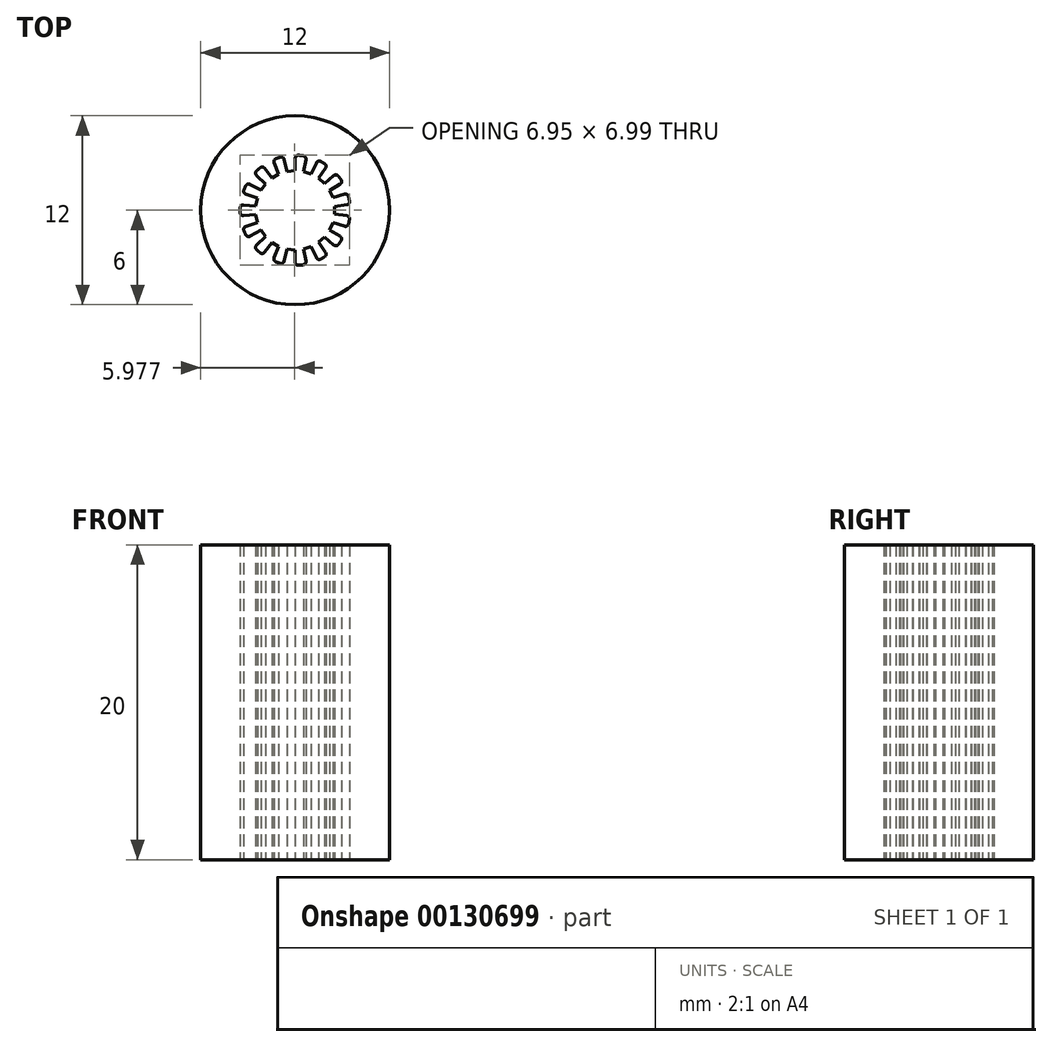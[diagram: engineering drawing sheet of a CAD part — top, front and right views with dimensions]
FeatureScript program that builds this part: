
annotation { "Feature Type Name" : "Feature", "Feature Type Description" : "" }
export const myFeature = defineFeature(function(context is Context, id is Id, definition is map)
    precondition{}
    {
        {
            var Q0;
            Q0=qCreatedBy(makeId("Top.planeOp"),FACE);
            var sketch = newSketch(context, id + "F0", { "sketchPlane" : qUnion([Q0])});
            skCircle(sketch, "E0", {"center": v(0, 0) * mm, "radius": 6 * mm});
            skLineSegment(sketch, "E1", {"start": v(2.5, 0) * mm, "end": v(3.5, 0) * mm, "construction": true});
            skLineSegment(sketch, "E2.right", {"start": v(2.5, 0.25) * mm, "end": v(2.5, -0.25) * mm});
            skPoint(sketch, "E2.middle", {"position": v(3, 0) * mm});
            skLineSegment(sketch, "E3", {"start": v(2.5, 0.25) * mm, "end": v(3.28, 0.35) * mm});
            skLineSegment(sketch, "E4", {"start": v(2.5, -0.25) * mm, "end": v(3.28, -0.35) * mm});
            skPoint(sketch, "E5.visualSharp", {"position": v(3.48, 0.37) * mm});
            skArc(sketch, "E5.filletArc", {"start": v(3.28, 0.35) * mm, "mid": v(3.41, 0.43) * mm, "end": v(3.45, 0.58) * mm});
            skPoint(sketch, "E6.visualSharp", {"position": v(3.48, -0.38) * mm});
            skArc(sketch, "E6.filletArc", {"start": v(3.45, -0.58) * mm, "mid": v(3.41, -0.43) * mm, "end": v(3.28, -0.35) * mm});
            skLineSegment(sketch, "E7.1.0", {"start": v(2.4, -0.8) * mm, "end": v(3.14, -1.01) * mm});
            skLineSegment(sketch, "E7.1.1", {"start": v(2.4, -0.8) * mm, "end": v(2.2, -1.25) * mm});
            skArc(sketch, "E7.1.2", {"start": v(2.92, -1.93) * mm, "mid": v(2.95, -1.78) * mm, "end": v(2.85, -1.65) * mm});
            skArc(sketch, "E7.1.3", {"start": v(3.14, -1.01) * mm, "mid": v(3.3, -1) * mm, "end": v(3.39, -0.87) * mm});
            skLineSegment(sketch, "E7.1.4", {"start": v(2.2, -1.25) * mm, "end": v(2.85, -1.65) * mm});
            skLineSegment(sketch, "E7.2.0", {"start": v(1.86, -1.7) * mm, "end": v(2.45, -2.2) * mm});
            skLineSegment(sketch, "E7.2.1", {"start": v(1.86, -1.7) * mm, "end": v(1.5, -2.03) * mm});
            skArc(sketch, "E7.2.2", {"start": v(1.88, -2.95) * mm, "mid": v(1.97, -2.82) * mm, "end": v(1.94, -2.67) * mm});
            skArc(sketch, "E7.2.3", {"start": v(2.45, -2.2) * mm, "mid": v(2.6, -2.25) * mm, "end": v(2.74, -2.18) * mm});
            skLineSegment(sketch, "E7.2.4", {"start": v(1.5, -2.03) * mm, "end": v(1.94, -2.67) * mm});
            skLineSegment(sketch, "E7.3.0", {"start": v(1.01, -2.3) * mm, "end": v(1.35, -3.01) * mm});
            skLineSegment(sketch, "E7.3.1", {"start": v(1.01, -2.3) * mm, "end": v(0.54, -2.46) * mm});
            skArc(sketch, "E7.3.2", {"start": v(0.51, -3.46) * mm, "mid": v(0.65, -3.38) * mm, "end": v(0.68, -3.23) * mm});
            skArc(sketch, "E7.3.3", {"start": v(1.35, -3.01) * mm, "mid": v(1.46, -3.12) * mm, "end": v(1.62, -3.1) * mm});
            skLineSegment(sketch, "E7.3.4", {"start": v(0.54, -2.46) * mm, "end": v(0.68, -3.23) * mm});
            skLineSegment(sketch, "E7.4.0", {"start": v(-0.01, -2.52) * mm, "end": v(0, -3.3) * mm});
            skLineSegment(sketch, "E7.4.1", {"start": v(-0.01, -2.52) * mm, "end": v(-0.51, -2.47) * mm});
            skArc(sketch, "E7.4.2", {"start": v(-0.94, -3.37) * mm, "mid": v(-0.78, -3.35) * mm, "end": v(-0.7, -3.23) * mm});
            skArc(sketch, "E7.4.3", {"start": v(0, -3.3) * mm, "mid": v(0.07, -3.44) * mm, "end": v(0.22, -3.5) * mm});
            skLineSegment(sketch, "E7.4.4", {"start": v(-0.51, -2.47) * mm, "end": v(-0.7, -3.23) * mm});
            skLineSegment(sketch, "E7.5.0", {"start": v(-1.04, -2.3) * mm, "end": v(-1.34, -3.01) * mm});
            skLineSegment(sketch, "E7.5.1", {"start": v(-1.04, -2.3) * mm, "end": v(-1.47, -2.05) * mm});
            skArc(sketch, "E7.5.2", {"start": v(-2.23, -2.7) * mm, "mid": v(-2.08, -2.74) * mm, "end": v(-1.94, -2.67) * mm});
            skArc(sketch, "E7.5.3", {"start": v(-1.34, -3.01) * mm, "mid": v(-1.34, -3.17) * mm, "end": v(-1.22, -3.28) * mm});
            skLineSegment(sketch, "E7.5.4", {"start": v(-1.47, -2.05) * mm, "end": v(-1.94, -2.67) * mm});
            skLineSegment(sketch, "E7.6.0", {"start": v(-1.88, -1.68) * mm, "end": v(-2.45, -2.21) * mm});
            skLineSegment(sketch, "E7.6.1", {"start": v(-1.88, -1.68) * mm, "end": v(-2.18, -1.27) * mm});
            skArc(sketch, "E7.6.2", {"start": v(-3.13, -1.56) * mm, "mid": v(-3.01, -1.66) * mm, "end": v(-2.86, -1.65) * mm});
            skArc(sketch, "E7.6.3", {"start": v(-2.45, -2.21) * mm, "mid": v(-2.51, -2.35) * mm, "end": v(-2.45, -2.5) * mm});
            skLineSegment(sketch, "E7.6.4", {"start": v(-2.18, -1.27) * mm, "end": v(-2.86, -1.65) * mm});
            skLineSegment(sketch, "E7.7.0", {"start": v(-2.4, -0.77) * mm, "end": v(-3.14, -1.02) * mm});
            skLineSegment(sketch, "E7.7.1", {"start": v(-2.4, -0.77) * mm, "end": v(-2.5, -0.28) * mm});
            skArc(sketch, "E7.7.2", {"start": v(-3.5, -0.15) * mm, "mid": v(-3.43, -0.3) * mm, "end": v(-3.28, -0.34) * mm});
            skArc(sketch, "E7.7.3", {"start": v(-3.14, -1.02) * mm, "mid": v(-3.25, -1.13) * mm, "end": v(-3.26, -1.29) * mm});
            skLineSegment(sketch, "E7.7.4", {"start": v(-2.5, -0.28) * mm, "end": v(-3.28, -0.34) * mm});
            skLineSegment(sketch, "E7.8.0", {"start": v(-2.5, 0.28) * mm, "end": v(-3.28, 0.34) * mm});
            skLineSegment(sketch, "E7.8.1", {"start": v(-2.5, 0.28) * mm, "end": v(-2.4, 0.77) * mm});
            skArc(sketch, "E7.8.2", {"start": v(-3.26, 1.29) * mm, "mid": v(-3.25, 1.13) * mm, "end": v(-3.14, 1.02) * mm});
            skArc(sketch, "E7.8.3", {"start": v(-3.28, 0.34) * mm, "mid": v(-3.43, 0.3) * mm, "end": v(-3.5, 0.15) * mm});
            skLineSegment(sketch, "E7.8.4", {"start": v(-2.4, 0.77) * mm, "end": v(-3.14, 1.02) * mm});
            skLineSegment(sketch, "E7.9.0", {"start": v(-2.18, 1.27) * mm, "end": v(-2.86, 1.65) * mm});
            skLineSegment(sketch, "E7.9.1", {"start": v(-2.18, 1.27) * mm, "end": v(-1.88, 1.68) * mm});
            skArc(sketch, "E7.9.2", {"start": v(-2.45, 2.5) * mm, "mid": v(-2.51, 2.35) * mm, "end": v(-2.45, 2.21) * mm});
            skArc(sketch, "E7.9.3", {"start": v(-2.86, 1.65) * mm, "mid": v(-3.01, 1.66) * mm, "end": v(-3.13, 1.56) * mm});
            skLineSegment(sketch, "E7.9.4", {"start": v(-1.88, 1.68) * mm, "end": v(-2.45, 2.21) * mm});
            skLineSegment(sketch, "E7.10.0", {"start": v(-1.47, 2.05) * mm, "end": v(-1.94, 2.67) * mm});
            skLineSegment(sketch, "E7.10.1", {"start": v(-1.47, 2.05) * mm, "end": v(-1.04, 2.3) * mm});
            skArc(sketch, "E7.10.2", {"start": v(-1.22, 3.28) * mm, "mid": v(-1.34, 3.17) * mm, "end": v(-1.34, 3.01) * mm});
            skArc(sketch, "E7.10.3", {"start": v(-1.94, 2.67) * mm, "mid": v(-2.08, 2.74) * mm, "end": v(-2.23, 2.7) * mm});
            skLineSegment(sketch, "E7.10.4", {"start": v(-1.04, 2.3) * mm, "end": v(-1.34, 3.01) * mm});
            skLineSegment(sketch, "E7.11.0", {"start": v(-0.51, 2.47) * mm, "end": v(-0.7, 3.23) * mm});
            skLineSegment(sketch, "E7.11.1", {"start": v(-0.51, 2.47) * mm, "end": v(-0.01, 2.52) * mm});
            skArc(sketch, "E7.11.2", {"start": v(0.22, 3.5) * mm, "mid": v(0.07, 3.44) * mm, "end": v(0, 3.3) * mm});
            skArc(sketch, "E7.11.3", {"start": v(-0.7, 3.23) * mm, "mid": v(-0.78, 3.35) * mm, "end": v(-0.94, 3.37) * mm});
            skLineSegment(sketch, "E7.11.4", {"start": v(-0.01, 2.52) * mm, "end": v(0, 3.3) * mm});
            skLineSegment(sketch, "E7.12.0", {"start": v(0.54, 2.46) * mm, "end": v(0.68, 3.23) * mm});
            skLineSegment(sketch, "E7.12.1", {"start": v(0.54, 2.46) * mm, "end": v(1.01, 2.3) * mm});
            skArc(sketch, "E7.12.2", {"start": v(1.62, 3.1) * mm, "mid": v(1.46, 3.12) * mm, "end": v(1.35, 3.01) * mm});
            skArc(sketch, "E7.12.3", {"start": v(0.68, 3.23) * mm, "mid": v(0.65, 3.38) * mm, "end": v(0.51, 3.46) * mm});
            skLineSegment(sketch, "E7.12.4", {"start": v(1.01, 2.3) * mm, "end": v(1.35, 3.01) * mm});
            skLineSegment(sketch, "E7.13.0", {"start": v(1.5, 2.03) * mm, "end": v(1.94, 2.67) * mm});
            skLineSegment(sketch, "E7.13.1", {"start": v(1.5, 2.03) * mm, "end": v(1.86, 1.7) * mm});
            skArc(sketch, "E7.13.2", {"start": v(2.74, 2.18) * mm, "mid": v(2.6, 2.25) * mm, "end": v(2.45, 2.2) * mm});
            skArc(sketch, "E7.13.3", {"start": v(1.94, 2.67) * mm, "mid": v(1.97, 2.82) * mm, "end": v(1.88, 2.95) * mm});
            skLineSegment(sketch, "E7.13.4", {"start": v(1.86, 1.7) * mm, "end": v(2.45, 2.2) * mm});
            skLineSegment(sketch, "E7.14.0", {"start": v(2.2, 1.25) * mm, "end": v(2.85, 1.65) * mm});
            skArc(sketch, "E7.14.2", {"start": v(3.39, 0.87) * mm, "mid": v(3.3, 1) * mm, "end": v(3.14, 1.01) * mm});
            skArc(sketch, "E7.14.3", {"start": v(2.85, 1.65) * mm, "mid": v(2.95, 1.78) * mm, "end": v(2.92, 1.93) * mm});
            skLineSegment(sketch, "E7.14.4", {"start": v(2.4, 0.8) * mm, "end": v(3.14, 1.01) * mm});
            skLineSegment(sketch, "E7.anchor1", {"start": v(0, 0) * mm, "end": v(2.5, -0.25) * mm, "construction": true});
            skLineSegment(sketch, "E7.anchor2", {"start": v(0, 0) * mm, "end": v(2.4, 0.8) * mm, "construction": true});
            skArc(sketch, "E8.trimOffspring", {"start": v(2.92, 1.93) * mm, "mid": v(2.83, 2.06) * mm, "end": v(2.74, 2.18) * mm});
            skArc(sketch, "E9.trimOffspring", {"start": v(0.51, 3.46) * mm, "mid": v(0.37, 3.48) * mm, "end": v(0.22, 3.5) * mm});
            skArc(sketch, "E10.trimOffspring", {"start": v(-2.23, 2.7) * mm, "mid": v(-2.34, 2.6) * mm, "end": v(-2.45, 2.5) * mm});
            skArc(sketch, "E11.trimOffspring", {"start": v(-0.94, 3.37) * mm, "mid": v(-1.08, 3.33) * mm, "end": v(-1.22, 3.28) * mm});
            skArc(sketch, "E12.trimOffspring", {"start": v(-3.13, 1.56) * mm, "mid": v(-3.2, 1.42) * mm, "end": v(-3.26, 1.29) * mm});
            skArc(sketch, "E13.trimOffspring", {"start": v(-3.5, 0.15) * mm, "mid": v(-3.5, 0) * mm, "end": v(-3.5, -0.15) * mm});
            skArc(sketch, "E14.trimOffspring", {"start": v(-3.26, -1.29) * mm, "mid": v(-3.2, -1.42) * mm, "end": v(-3.13, -1.56) * mm});
            skArc(sketch, "E15.trimOffspring", {"start": v(-2.45, -2.5) * mm, "mid": v(-2.34, -2.6) * mm, "end": v(-2.23, -2.7) * mm});
            skArc(sketch, "E16.trimOffspring", {"start": v(-1.22, -3.28) * mm, "mid": v(-1.08, -3.33) * mm, "end": v(-0.94, -3.37) * mm});
            skArc(sketch, "E17.trimOffspring", {"start": v(0.22, -3.5) * mm, "mid": v(0.37, -3.48) * mm, "end": v(0.51, -3.46) * mm});
            skArc(sketch, "E18.trimOffspring", {"start": v(1.62, -3.1) * mm, "mid": v(1.75, -3.03) * mm, "end": v(1.88, -2.95) * mm});
            skArc(sketch, "E19.trimOffspring", {"start": v(2.74, -2.18) * mm, "mid": v(2.83, -2.06) * mm, "end": v(2.92, -1.93) * mm});
            skArc(sketch, "E20.trimOffspring", {"start": v(3.39, -0.87) * mm, "mid": v(3.42, -0.73) * mm, "end": v(3.45, -0.58) * mm});
            skArc(sketch, "E21", {"start": v(3.39, 0.87) * mm, "mid": v(3.42, 0.73) * mm, "end": v(3.45, 0.58) * mm});
            skArc(sketch, "E22", {"start": v(1.62, 3.1) * mm, "mid": v(1.75, 3.03) * mm, "end": v(1.88, 2.95) * mm});
            skLineSegment(sketch, "E23", {"start": v(2.2, 1.25) * mm, "end": v(2.4, 0.8) * mm});
            skSolve(sketch);
        }
        {
            var Q0;
            Q0=makeQuery(id+"F0.imprint","IMPRINT",FACE,{"disambiguationData":[TD([[makeQuery(id+"F0.imprint","IMPRINT",EDGE,{"derivedFrom":sQuery(id+"F0.wireOp",EDGE,"E0")}),1.0]])]});
            extrude(context, id + "F1", {"entities" : qUnion([Q0]), "depth" : 20 * mm});
        }
    });
